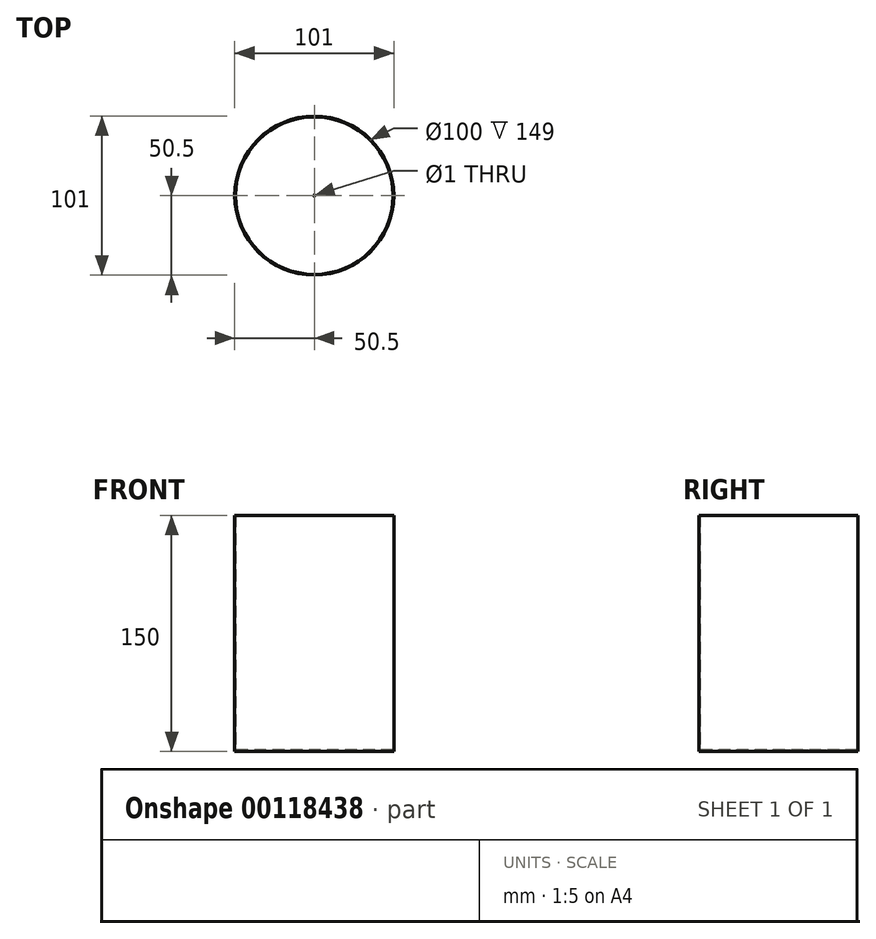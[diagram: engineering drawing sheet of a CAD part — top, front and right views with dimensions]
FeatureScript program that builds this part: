
annotation { "Feature Type Name" : "Feature", "Feature Type Description" : "" }
export const myFeature = defineFeature(function(context is Context, id is Id, definition is map)
    precondition{}
    {
        {
            var Q0;
            Q0=qCreatedBy(makeId("Top.planeOp"),FACE);
            var sketch = newSketch(context, id + "F0", { "sketchPlane" : qUnion([Q0])});
            skCircle(sketch, "E0", {"center": v(0, 0) * mm, "radius": 50 * mm});
            skCircle(sketch, "E1", {"center": v(0, 0) * mm, "radius": 50.5 * mm});
            skSolve(sketch);
        }
        {
            var Q0;
            Q0=makeQuery(id+"F0.imprint","IMPRINT",FACE,{"disambiguationData":[TD([[makeQuery(id+"F0.imprint","IMPRINT",EDGE,{"derivedFrom":sQuery(id+"F0.wireOp",EDGE,"E1")}),1.0]])]});
            extrude(context, id + "F1", {"entities" : qUnion([Q0]), "depth" : 150 * mm});
        }
        {
            var Q0;
            Q0=qCreatedBy(makeId("Top.planeOp"),FACE);
            var sketch = newSketch(context, id + "F2", { "sketchPlane" : qUnion([Q0])});
            skCircle(sketch, "E2", {"center": v(0, 0) * mm, "radius": 50.5 * mm});
            skCircle(sketch, "E3", {"center": v(0, 0) * mm, "radius": 0.5 * mm});
            skSolve(sketch);
        }
        {
            var Q0;
            Q0=makeQuery(id+"F2.imprint","IMPRINT",FACE,{"disambiguationData":[TD([[makeQuery(id+"F2.imprint","IMPRINT",EDGE,{"derivedFrom":sQuery(id+"F2.wireOp",EDGE,"E2")}),1.0]])]});
            extrude(context, id + "F3", {"entities" : qUnion([Q0]), "operationType" : NewBodyOperationType.ADD, "depth" : 1 * mm});
        }
    });
